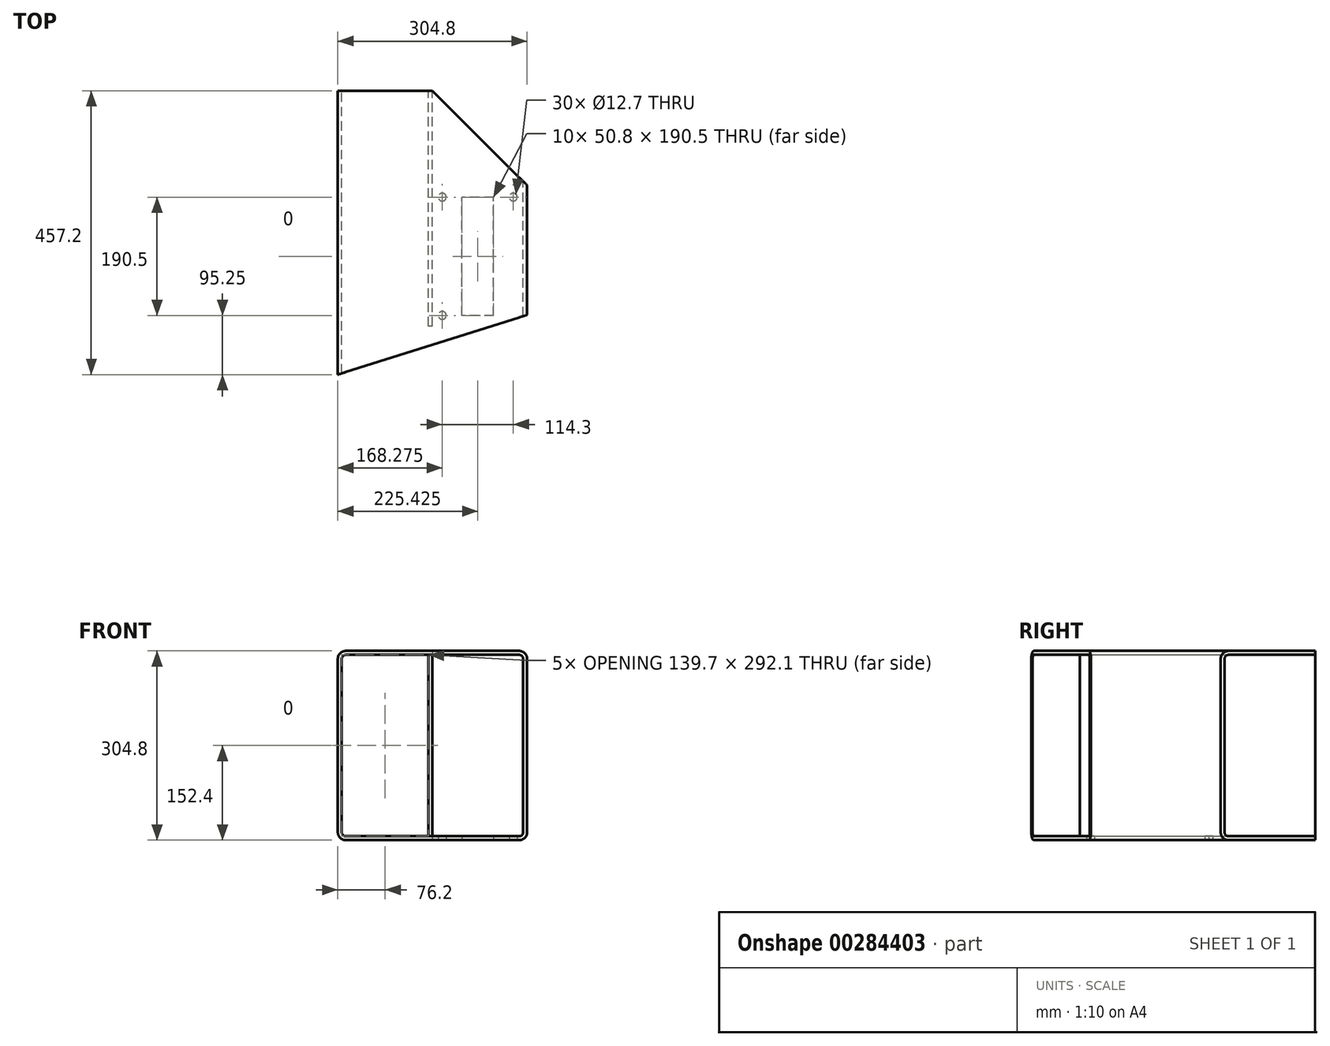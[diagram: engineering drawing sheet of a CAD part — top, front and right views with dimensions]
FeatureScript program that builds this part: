
annotation { "Feature Type Name" : "Feature", "Feature Type Description" : "" }
export const myFeature = defineFeature(function(context is Context, id is Id, definition is map)
    precondition{}
    {
        {
            var Q0;
            Q0=qCreatedBy(makeId("Front.planeOp"),FACE);
            var sketch = newSketch(context, id + "F0", { "sketchPlane" : qUnion([Q0])});
            skLineSegment(sketch, "E0.bottom", {"start": v(139.7, 146.05) * mm, "end": v(-139.7, 146.05) * mm});
            skLineSegment(sketch, "E0.top", {"start": v(139.7, -146.05) * mm, "end": v(-139.7, -146.05) * mm});
            skLineSegment(sketch, "E0.left", {"start": v(146.05, 139.7) * mm, "end": v(146.05, -139.7) * mm});
            skLineSegment(sketch, "E0.right", {"start": v(-146.05, 139.7) * mm, "end": v(-146.05, -139.7) * mm});
            skPoint(sketch, "E0.middle", {"position": v(0, 0) * mm});
            skPoint(sketch, "E1.visualSharp", {"position": v(-146.05, 146.05) * mm});
            skArc(sketch, "E1.filletArc", {"start": v(-139.7, 146.05) * mm, "mid": v(-144.2, 144.2) * mm, "end": v(-146.05, 139.7) * mm});
            skPoint(sketch, "E2.visualSharp", {"position": v(146.05, 146.05) * mm});
            skArc(sketch, "E2.filletArc", {"start": v(146.05, 139.7) * mm, "mid": v(144.2, 144.2) * mm, "end": v(139.7, 146.05) * mm});
            skPoint(sketch, "E3.visualSharp", {"position": v(146.05, -146.05) * mm});
            skArc(sketch, "E3.filletArc", {"start": v(139.7, -146.05) * mm, "mid": v(144.2, -144.2) * mm, "end": v(146.05, -139.7) * mm});
            skPoint(sketch, "E4.visualSharp", {"position": v(-146.05, -146.05) * mm});
            skArc(sketch, "E4.filletArc", {"start": v(-146.05, -139.7) * mm, "mid": v(-144.2, -144.2) * mm, "end": v(-139.7, -146.05) * mm});
            skArc(sketch, "E5.0", {"start": v(139.7, -152.4) * mm, "mid": v(148.68, -148.68) * mm, "end": v(152.4, -139.7) * mm});
            skLineSegment(sketch, "E5.1", {"start": v(152.4, 139.7) * mm, "end": v(152.4, -139.7) * mm});
            skLineSegment(sketch, "E5.2", {"start": v(139.7, -152.4) * mm, "end": v(-139.7, -152.4) * mm});
            skArc(sketch, "E5.3", {"start": v(152.4, 139.7) * mm, "mid": v(148.68, 148.68) * mm, "end": v(139.7, 152.4) * mm});
            skArc(sketch, "E5.4", {"start": v(-152.4, -139.7) * mm, "mid": v(-148.68, -148.68) * mm, "end": v(-139.7, -152.4) * mm});
            skLineSegment(sketch, "E5.5", {"start": v(-152.4, 139.7) * mm, "end": v(-152.4, -139.7) * mm});
            skArc(sketch, "E5.6", {"start": v(-139.7, 152.4) * mm, "mid": v(-148.68, 148.68) * mm, "end": v(-152.4, 139.7) * mm});
            skLineSegment(sketch, "E5.7", {"start": v(139.7, 152.4) * mm, "end": v(-139.7, 152.4) * mm});
            skLineSegment(sketch, "E6", {"start": v(0, 146.05) * mm, "end": v(0, -146.05) * mm});
            skLineSegment(sketch, "E7.0", {"start": v(-6.35, 146.05) * mm, "end": v(-6.35, -146.05) * mm});
            skSolve(sketch);
        }
        {
            var Q0;
            Q0=makeQuery(id+"F0.imprint","IMPRINT",FACE,{"disambiguationData":[TD([[makeQuery(id+"F0.imprint","IMPRINT",EDGE,{"derivedFrom":sQuery(id+"F0.wireOp",EDGE,"E0.bottom")}),-1.0]])]});
            var Q1;
            {var subQ0=sQuery(id+"F0.wireOp",EDGE,"E6");Q1=makeQuery(id+"F0.imprint","IMPRINT",FACE,{"disambiguationData":[TD([[makeQuery(id+"F0.imprint","IMPRINT",EDGE,{"derivedFrom":subQ0}),-1.0]])]});}
            extrude(context, id + "F1", {"entities" : qUnion([Q0, Q1]), "depth" : 457.2 * mm});
        }
        {
            var Q0;
            Q0=makeQuery(id+"F1.opExtrude","SWEPT_FACE",FACE,{"disambiguationData":[OSD([sQuery(id+"F0.wireOp",EDGE,"E5.2")])]});
            var sketch = newSketch(context, id + "F2", { "sketchPlane" : qUnion([Q0])});
            skPoint(sketch, "E8.middle", {"position": v(73.02, 266.7) * mm});
            skCircle(sketch, "E9", {"center": v(15.87, 361.95) * mm, "radius": 6.35 * mm});
            skLineSegment(sketch, "E10.bottom", {"start": v(149.22, 374.65) * mm, "end": v(-3.18, 374.65) * mm});
            skLineSegment(sketch, "E10.top", {"start": v(149.22, 158.75) * mm, "end": v(-3.18, 158.75) * mm});
            skLineSegment(sketch, "E10.left", {"start": v(149.22, 374.65) * mm, "end": v(149.22, 158.75) * mm});
            skLineSegment(sketch, "E10.right", {"start": v(-3.18, 374.65) * mm, "end": v(-3.18, 158.75) * mm});
            skLineSegment(sketch, "E11.0", {"start": v(139.7, 457.2) * mm, "end": v(-139.7, 457.2) * mm});
            skLineSegment(sketch, "E12.0", {"start": v(139.7, 457.2) * mm, "end": v(152.4, 457.2) * mm});
            skLineSegment(sketch, "E13", {"start": v(0, 266.7) * mm, "end": v(152.4, 266.7) * mm, "construction": true});
            skLineSegment(sketch, "E14.bottom", {"start": v(98.42, 361.95) * mm, "end": v(47.62, 361.95) * mm});
            skLineSegment(sketch, "E14.top", {"start": v(98.42, 171.45) * mm, "end": v(47.62, 171.45) * mm});
            skLineSegment(sketch, "E14.left", {"start": v(98.42, 361.95) * mm, "end": v(98.42, 171.45) * mm});
            skLineSegment(sketch, "E14.right", {"start": v(47.62, 361.95) * mm, "end": v(47.62, 171.45) * mm});
            skCircle(sketch, "E15.0.1.0", {"center": v(15.87, 171.45) * mm, "radius": 6.35 * mm});
            skCircle(sketch, "E15.1.0.0", {"center": v(130.17, 361.95) * mm, "radius": 6.35 * mm});
            skCircle(sketch, "E15.1.1.0", {"center": v(130.17, 171.45) * mm, "radius": 6.35 * mm});
            skLineSegment(sketch, "E15.direction1", {"start": v(15.87, 361.95) * mm, "end": v(130.17, 361.95) * mm, "construction": true});
            skLineSegment(sketch, "E15.direction2", {"start": v(15.87, 361.95) * mm, "end": v(15.87, 171.45) * mm, "construction": true});
            skLineSegment(sketch, "E16.0", {"start": v(0, 457.2) * mm, "end": v(0, 0) * mm});
            skLineSegment(sketch, "E17.0", {"start": v(152.4, 457.2) * mm, "end": v(152.4, 0) * mm});
            skSolve(sketch);
        }
        {
            var Q0;
            Q0=makeQuery(id+"F1.opExtrude","SWEPT_FACE",FACE,{"disambiguationData":[OSD([sQuery(id+"F0.wireOp",EDGE,"E5.2")])]});
            var sketch = newSketch(context, id + "F3", { "sketchPlane" : qUnion([Q0])});
            skLineSegment(sketch, "E18.0", {"start": v(152.4, 457.2) * mm, "end": v(152.4, 0) * mm});
            skLineSegment(sketch, "E19.0", {"start": v(139.7, 0) * mm, "end": v(-139.7, 0) * mm});
            skLineSegment(sketch, "E20.0", {"start": v(139.7, 0) * mm, "end": v(152.4, 0) * mm});
            skLineSegment(sketch, "E21", {"start": v(152.4, 143.42) * mm, "end": v(8.98, 0) * mm});
            skLineSegment(sketch, "E22.0", {"start": v(152.4, 152.4) * mm, "end": v(0, 0) * mm});
            skLineSegment(sketch, "E23.0", {"start": v(-152.4, 457.2) * mm, "end": v(-152.4, 0) * mm});
            skLineSegment(sketch, "E24.0", {"start": v(139.7, 457.2) * mm, "end": v(-139.7, 457.2) * mm});
            skLineSegment(sketch, "E25.0", {"start": v(139.7, 457.2) * mm, "end": v(152.4, 457.2) * mm});
            skLineSegment(sketch, "E26.0", {"start": v(-152.4, 457.2) * mm, "end": v(-139.7, 457.2) * mm});
            skLineSegment(sketch, "E27", {"start": v(-152.4, 457.2) * mm, "end": v(152.4, 361.1) * mm});
            skSolve(sketch);
        }
        {
            var Q0;
            {var subQ0=sQuery(id+"F3.wireOp",EDGE,"E21");var subQ1=sQuery(id+"F3.wireOp",EDGE,"E18.0");var subQ2=makeQuery(id+"F3.imprint","INTERSECT",VERTEX,{"derivedFrom":[subQ1,subQ0]});Q0=makeQuery(id+"F3.imprint","IMPRINT",FACE,{"disambiguationData":[TD([[makeQuery(id+"F3.imprint","IMPRINT",EDGE,{"disambiguationData":[TD([[subQ2,1.0]])],"derivedFrom":subQ1}),-1.0]])]});}
            var Q1;
            {var subQ0=sQuery(id+"F3.wireOp",EDGE,"E21");var subQ1=sQuery(id+"F3.wireOp",EDGE,"E19.0");var subQ2=makeQuery(id+"F3.imprint","INTERSECT",VERTEX,{"derivedFrom":[subQ1,subQ0]});Q1=makeQuery(id+"F3.imprint","IMPRINT",FACE,{"disambiguationData":[TD([[makeQuery(id+"F3.imprint","IMPRINT",EDGE,{"disambiguationData":[TD([[subQ2,-1.0]])],"derivedFrom":subQ1}),-1.0]])]});}
            var Q2;
            {var subQ0=sQuery(id+"F3.wireOp",EDGE,"E19.0");var subQ3=sQuery(id+"F3.wireOp",EDGE,"E21");var subQ4=makeQuery(id+"F3.imprint","INTERSECT",VERTEX,{"derivedFrom":[subQ0,subQ3]});Q2=makeQuery(id+"F3.imprint","IMPRINT",FACE,{"disambiguationData":[TD([[makeQuery(id+"F3.imprint","IMPRINT",EDGE,{"disambiguationData":[TD([[subQ4,1.0]])],"derivedFrom":subQ3}),1.0]])]});}
            var Q3;
            {var subQ0=sQuery(id+"F3.wireOp",EDGE,"E20.0");Q3=makeQuery(id+"F3.imprint","IMPRINT",FACE,{"disambiguationData":[TD([[makeQuery(id+"F3.imprint","IMPRINT",EDGE,{"derivedFrom":subQ0}),1.0]])]});}
            var Q4;
            {var subQ0=sQuery(id+"F3.wireOp",EDGE,"E24.0");Q4=makeQuery(id+"F3.imprint","IMPRINT",FACE,{"disambiguationData":[TD([[makeQuery(id+"F3.imprint","IMPRINT",EDGE,{"derivedFrom":subQ0}),1.0]])]});}
            var Q5;
            {var subQ0=sQuery(id+"F3.wireOp",EDGE,"E26.0");Q5=makeQuery(id+"F3.imprint","IMPRINT",FACE,{"disambiguationData":[TD([[makeQuery(id+"F3.imprint","IMPRINT",EDGE,{"derivedFrom":subQ0}),-1.0]])]});}
            var Q6;
            {var subQ0=sQuery(id+"F3.wireOp",EDGE,"E25.0");Q6=makeQuery(id+"F3.imprint","IMPRINT",FACE,{"disambiguationData":[TD([[makeQuery(id+"F3.imprint","IMPRINT",EDGE,{"derivedFrom":subQ0}),-1.0]])]});}
            extrude(context, id + "F4", {"entities" : qUnion([Q0, Q1, Q2, Q3, Q4, Q5, Q6]), "operationType" : NewBodyOperationType.REMOVE, "endBound" : BoundingType.THROUGH_ALL, "oppositeDirection" : true, "depth" : 25.4 * mm});
        }
        {
            var Q0;
            Q0=makeQuery(id+"F2.imprint","IMPRINT",FACE,{"disambiguationData":[TD([[makeQuery(id+"F2.imprint","IMPRINT",EDGE,{"derivedFrom":sQuery(id+"F2.wireOp",EDGE,"E14.bottom")}),1.0]])]});
            var Q1;
            Q1=makeQuery(id+"F2.imprint","IMPRINT",FACE,{"disambiguationData":[TD([[makeQuery(id+"F2.imprint","IMPRINT",EDGE,{"derivedFrom":sQuery(id+"F2.wireOp",EDGE,"E15.0.1.0")}),1.0]])]});
            var Q2;
            Q2=makeQuery(id+"F2.imprint","IMPRINT",FACE,{"disambiguationData":[TD([[makeQuery(id+"F2.imprint","IMPRINT",EDGE,{"derivedFrom":sQuery(id+"F2.wireOp",EDGE,"E15.1.1.0")}),1.0]])]});
            var Q3;
            Q3=makeQuery(id+"F2.imprint","IMPRINT",FACE,{"disambiguationData":[TD([[makeQuery(id+"F2.imprint","IMPRINT",EDGE,{"derivedFrom":sQuery(id+"F2.wireOp",EDGE,"E9")}),1.0]])]});
            extrude(context, id + "F5", {"entities" : qUnion([Q0, Q1, Q2, Q3]), "operationType" : NewBodyOperationType.REMOVE, "oppositeDirection" : true, "depth" : 6.35 * mm});
        }
        {
            var Q0;
            Q0=makeQuery(id+"F1.opExtrude","SWEPT_FACE",FACE,{"disambiguationData":[OSD([sQuery(id+"F0.wireOp",EDGE,"E7.0")])]});
            var sketch = newSketch(context, id + "F6", { "sketchPlane" : qUnion([Q0])});
            skLineSegment(sketch, "E28.0", {"start": v(411.15, -146.05) * mm, "end": v(411.15, 146.05) * mm});
            skLineSegment(sketch, "E29.0", {"start": v(411.15, -146.05) * mm, "end": v(0, -146.05) * mm});
            skLineSegment(sketch, "E30.0", {"start": v(411.15, 146.05) * mm, "end": v(0, 146.05) * mm});
            skLineSegment(sketch, "E31", {"start": v(379.4, 146.05) * mm, "end": v(379.4, -146.05) * mm});
            skPoint(sketch, "E31.endSnap0", {"position": v(205.58, -146.05) * mm});
            skSolve(sketch);
        }
        {
            var Q0;
            Q0 = qSketchRegion(id + "F6", true);
            extrude(context, id + "F7", {"entities" : qUnion([Q0]), "operationType" : NewBodyOperationType.REMOVE, "endBound" : BoundingType.UP_TO_NEXT, "oppositeDirection" : true, "depth" : 25.4 * mm});
        }
    });
